# Revit family: BuroSeating_Konfurb Orbit HB_Pedestal
name_source: partatom
category: Furniture
units: mm (PartAtom-declared; Revit-internal decimal feet)

## family parameters
Always vertical = Yes
Cut with Voids When Loaded = No
OmniClass Number = 23.40.70.14.64.11
OmniClass Title = Office Furniture
Room Calculation Point = No
Shared = Yes
Work Plane-Based = No

## types (1)
- Konfurb Orbit Pedestal High Back
    Assembly Code = E2020
    BaseFrameMaterial = BuroSeating_Metal_Chrome_Semi-Polished
    Default Elevation = 0 mm  [stored 0 ft]
    Description = Konfurb Orbit Pedestal High Back
    FeetMaterial = BuroSeating_Steel_Dark Grey
    FrameMaterial = BuroSeating_Steel_Dark Grey
    Manufacturer = Buro Seating
    Model = KON181
    NominalDepth = 720 mm  [stored 2.3622 ft]
    NominalHeight = 1285 mm  [stored 4.21588 ft]
    NominalWidth = 655 mm  [stored 2.14895 ft]
    ProductGroup = Orbit
    ProductPageURL AU = https://buroseating.com
    ProductPageURL NZ = https://buroseating.co.nz
    ProductRange = Konfurb
    SeatArms = No
    SeatBackHeght = 840 mm  [stored 2.75591 ft]
    SeatDepth = 470 mm  [stored 1.54199 ft]
    SeatHeadRest = No
    SeatHeight = 445 mm  [stored 1.45997 ft]
    SeatWidth = 515 mm  [stored 1.68963 ft]
    Type Comments = Seat Height 435 High
    URL = https://buroseating.co.nz
    URL AU = https://buroseating.com
    WarrantyDescription = Full 5 year guarantee (excluding upholstery)

note: [stored X ft] marks values corroborated as IEEE doubles in the binary element streams (Revit-internal decimal feet)

## geometry (parser evidence)
native form markers: Sweep x5
no freeform markers — native parametric forms only
